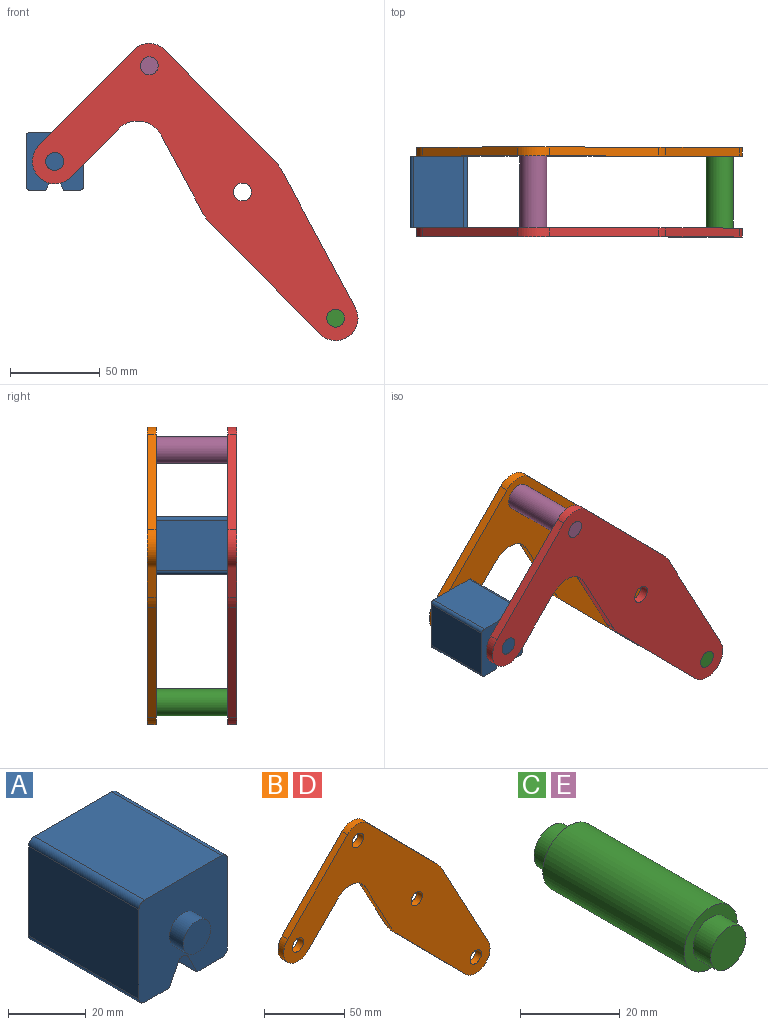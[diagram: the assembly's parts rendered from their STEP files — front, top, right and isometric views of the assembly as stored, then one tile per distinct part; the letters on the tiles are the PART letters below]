
ASSEMBLY  parts=5 mates=3
PART A: 18 faces, bbox 32.1x50x32.1 mm
  f0: plane 40x28.08mm, normal (1,0,0), area 1123.1mm2, adj f4,f10,f13,f14
  f1: plane 40x9.04mm, normal (0,0,-1), area 361.6mm2, adj f2,f4,f10,f14
  f2: plane 40x6.42mm, normal (-0.89,0,-0.45), area 287.2mm2, adj f1,f4,f10,f15
  f3: plane 40x6.42mm, normal (0.89,0,-0.45), area 287.2mm2, adj f4,f5,f10,f15
  f4: plane 32.08x32.08mm, normal (0,-1,0), area 900.6mm2, adj f0,f1,f2,f3,f5,f6,f7,f9
  f5: plane 40x9.04mm, normal (0,0,-1), area 361.6mm2, adj f3,f4,f10,f16
  f6: plane 40x28.08mm, normal (0,0,1), area 1123.1mm2, adj f4,f10,f13,f17
  f7: plane 40x28.08mm, normal (-1,0,0), area 1123.1mm2, adj f4,f10,f16,f17
  f8: plane 10x10mm, normal (0,-1,0), area 78.5mm2, adj f9
  f9: cylinder r=5mm len=10mm, axis (0,1,0), area 157.1mm2, adj f4,f8
  f10: plane 32.08x32.08mm, normal (0,1,0), area 900.6mm2, adj f0,f1,f2,f3,f5,f6,f7,f12
  f11: plane 10x10mm, normal (0,1,0), area 78.5mm2, adj f12
  f12: cylinder r=5mm len=10mm, axis (0,-1,0), area 157.1mm2, adj f10,f11
  f13: cylinder r=2mm len=40mm, axis (0,1,0), area 125.7mm2, adj f0,f4,f6,f10
  f14: cylinder r=2mm len=40mm, axis (0,-1,0), area 125.7mm2, adj f0,f1,f4,f10
  f15: cylinder r=2mm len=40mm, axis (0,1,0), area 177.1mm2, adj f2,f3,f4,f10
  f16: cylinder r=2mm len=40mm, axis (0,1,0), area 125.7mm2, adj f4,f5,f7,f10
  f17: cylinder r=2mm len=40mm, axis (0,-1,0), area 125.7mm2, adj f4,f6,f7,f10
PART B: 18 faces, bbox 181.7x5x165.8 mm
  f0: plane 43.49x23.35mm, normal (-0.88,0,-0.47), area 246.8mm2, adj f1,f14,f16,f17
  f1: cylinder r=25mm len=5.75mm, axis (0,1,0), area 35.8mm2, adj f0,f2,f16,f17
  f2: plane 61.6x60.87mm, normal (-0.71,0,-0.7), area 433mm2, adj f1,f3,f16,f17
  f3: cylinder r=12.5mm len=21.39mm, axis (0,1,0), area 178.4mm2, adj f2,f4,f16,f17
  f4: plane 76.3x40.96mm, normal (0.88,0,0.47), area 433mm2, adj f3,f5,f16,f17
  f5: cylinder r=25mm len=5.75mm, axis (0,1,0), area 35.8mm2, adj f4,f6,f16,f17
  f6: plane 61.6x60.87mm, normal (0.71,0,0.7), area 433mm2, adj f5,f7,f16,f17
  f7: cylinder r=12.5mm len=17.78mm, axis (0,1,0), area 98.9mm2, adj f6,f8,f16,f17
  f8: plane 53.35x52.71mm, normal (-0.71,0,0.7), area 375mm2, adj f7,f9,f16,f17
  f9: cylinder r=12.5mm len=21.39mm, axis (0,1,0), area 196.3mm2, adj f8,f10,f16,f17
  f10: plane 26.86x26.54mm, normal (0.71,0,-0.7), area 188.8mm2, adj f9,f14,f16,f17
  f11: cylinder r=5mm len=10mm, axis (0,1,0), area 157.1mm2, adj f16,f17
  f12: cylinder r=5mm len=10mm, axis (0,1,0), area 157.1mm2, adj f16,f17
  f13: cylinder r=5mm len=10mm, axis (0,1,0), area 157.1mm2, adj f16,f17
  f14: cylinder r=15mm len=23.89mm, axis (0,1,0), area 140.2mm2, adj f0,f10,f16,f17
  f15: cylinder r=5mm len=10mm, axis (0,1,0), area 157.1mm2, adj f16,f17
  f16: plane 181.66x165.78mm, normal (0,-1,0), area 8710.1mm2, adj f0,f1,f2,f3,f4,f5,f6,f7
  f17: plane 181.66x165.78mm, normal (0,1,0), area 8710.1mm2, adj f0,f1,f2,f3,f4,f5,f6,f7
PART C: 7 faces, bbox 15x50x15 mm
  f0: cylinder r=7.5mm len=40mm, axis (0,-1,0), area 1885mm2, adj f2,f5
  f1: cylinder r=5mm len=10mm, axis (0,1,0), area 157.1mm2, adj f2,f3
  f2: plane 15x15mm, normal (0,-1,0), area 98.2mm2, adj f0,f1
  f3: plane 10x10mm, normal (0,-1,0), area 78.5mm2, adj f1
  f4: cylinder r=5mm len=10mm, axis (0,-1,0), area 157.1mm2, adj f5,f6
  f5: plane 15x15mm, normal (0,1,0), area 98.2mm2, adj f0,f4
  f6: plane 10x10mm, normal (0,1,0), area 78.5mm2, adj f4
PART D: same geometry as B
PART E: same geometry as C
PLACE A t=(41.9,-1.13,60.52)mm
PLACE B t=(41.9,43.87,60.52)mm
PLACE C t=(145.85,-1.13,-80.26)mm
PLACE D t=(41.9,-1.13,60.52)mm fixed
PLACE E t=(41.9,-1.13,60.52)mm
MATE fastened D.f3 <-> C.f0  axis (0,-1,0) through (93.88,-6.13,-9.87)mm
MATE fastened E.f0 <-> B.f7  axis (0,1,0) through (-10.07,43.87,130.91)mm
MATE revolute A.f9 <-> D.f9  axis (0,-1,0) through (-62.79,-6.13,77.56)mm
